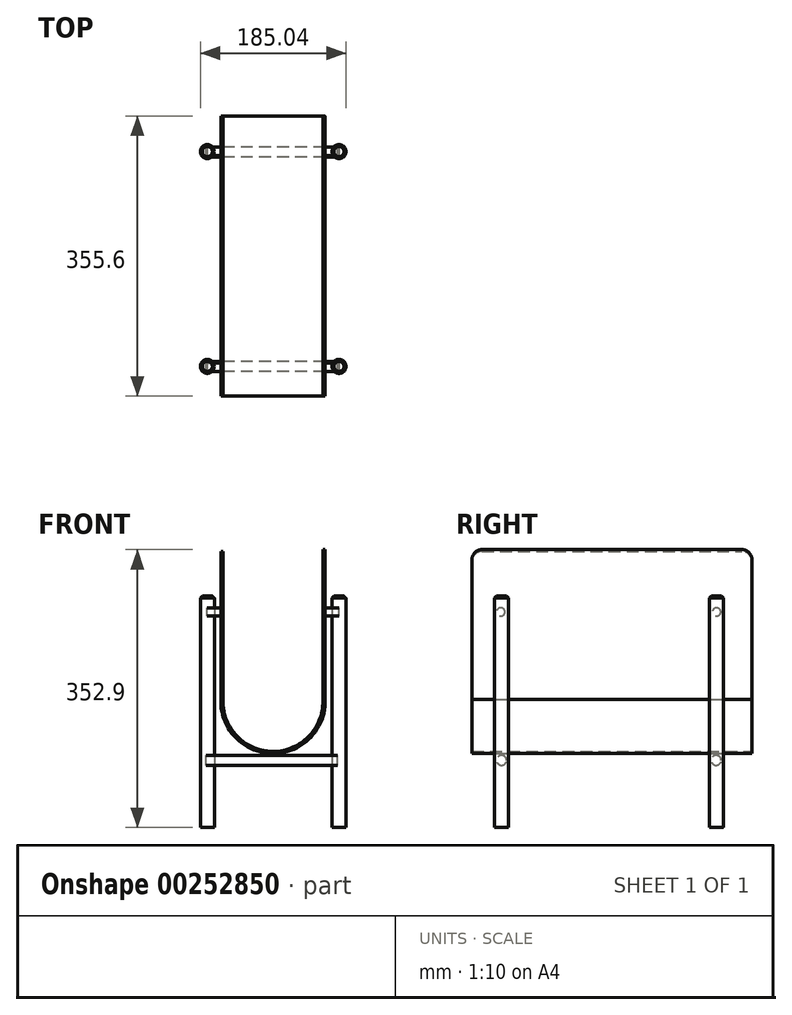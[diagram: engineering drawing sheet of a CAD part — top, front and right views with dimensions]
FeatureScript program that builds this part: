
annotation { "Feature Type Name" : "Feature", "Feature Type Description" : "" }
export const myFeature = defineFeature(function(context is Context, id is Id, definition is map)
    precondition{}
    {
        {
            var Q0;
            Q0=qCreatedBy(makeId("Front.planeOp"),FACE);
            var sketch = newSketch(context, id + "F0", { "sketchPlane" : qUnion([Q0])});
            skArc(sketch, "E0", {"start": v(-63.5, 63.5) * mm, "mid": v(1.2, 0.01) * mm, "end": v(63.46, 65.88) * mm});
            skLineSegment(sketch, "E1", {"start": v(-63.5, 63.5) * mm, "end": v(-63.5, 254) * mm});
            skLineSegment(sketch, "E2", {"start": v(63.46, 65.88) * mm, "end": v(63.46, 256.38) * mm});
            skLineSegment(sketch, "E3.0", {"start": v(-66.3, 63.5) * mm, "end": v(-66.3, 254) * mm});
            skArc(sketch, "E3.1", {"start": v(-66.3, 63.5) * mm, "mid": v(1.22, -2.78) * mm, "end": v(66.25, 65.94) * mm});
            skLineSegment(sketch, "E3.2", {"start": v(66.25, 65.94) * mm, "end": v(66.25, 256.32) * mm});
            skLineSegment(sketch, "E4", {"start": v(-66.3, 254) * mm, "end": v(-63.5, 254) * mm});
            skLineSegment(sketch, "E5", {"start": v(63.46, 256.38) * mm, "end": v(66.25, 256.32) * mm});
            skSolve(sketch);
        }
        {
            var Q0;
            Q0=makeQuery(id+"F0.imprint","IMPRINT",FACE,{"disambiguationData":[TD([[makeQuery(id+"F0.imprint","IMPRINT",EDGE,{"derivedFrom":sQuery(id+"F0.wireOp",EDGE,"E0")}),-1.0]])]});
            extrude(context, id + "F1", {"entities" : qUnion([Q0]), "depth" : 355.6 * mm});
        }
        {
            var Q0;
            Q0=makeQuery(id+"F1.opExtrude","CAP_EDGE",EDGE,{"disambiguationData":[OSD([sQuery(id+"F0.wireOp",EDGE,"E4")])],"isStart":false});
            var Q1;
            Q1=makeQuery(id+"F1.opExtrude","CAP_EDGE",EDGE,{"disambiguationData":[OSD([sQuery(id+"F0.wireOp",EDGE,"E5")])],"isStart":false});
            var Q2;
            Q2=makeQuery(id+"F1.opExtrude","CAP_EDGE",EDGE,{"disambiguationData":[OSD([sQuery(id+"F0.wireOp",EDGE,"E4")])],"isStart":true});
            var Q3;
            Q3=makeQuery(id+"F1.opExtrude","CAP_EDGE",EDGE,{"disambiguationData":[OSD([sQuery(id+"F0.wireOp",EDGE,"E5")])],"isStart":true});
            fillet(context, id + "F2", {"entities" : qUnion([Q0, Q1, Q2, Q3]), "radius" : 12.7 * mm, "tangentPropagation" : true, "allowEdgeOverflow" : false});
        }
        {
            var Q0;
            Q0=qCreatedBy(makeId("Top.planeOp"),FACE);
            var sketch = newSketch(context, id + "F3", { "sketchPlane" : qUnion([Q0])});
            skCircle(sketch, "E6", {"center": v(-83.41, -45.01) * mm, "radius": 8.9 * mm});
            skCircle(sketch, "E7", {"center": v(83.85, -45.01) * mm, "radius": 8.9 * mm});
            skCircle(sketch, "E8", {"center": v(-83.41, -317.88) * mm, "radius": 8.9 * mm});
            skCircle(sketch, "E9", {"center": v(83.85, -317.88) * mm, "radius": 8.9 * mm});
            skSolve(sketch);
        }
        {
            var Q0;
            Q0=makeQuery(id+"F3.imprint","IMPRINT",FACE,{"disambiguationData":[TD([[makeQuery(id+"F3.imprint","IMPRINT",EDGE,{"derivedFrom":sQuery(id+"F3.wireOp",EDGE,"E6")}),1.0]])]});
            var Q1;
            Q1=makeQuery(id+"F3.imprint","IMPRINT",FACE,{"disambiguationData":[TD([[makeQuery(id+"F3.imprint","IMPRINT",EDGE,{"derivedFrom":sQuery(id+"F3.wireOp",EDGE,"E8")}),1.0]])]});
            var Q2;
            Q2=makeQuery(id+"F3.imprint","IMPRINT",FACE,{"disambiguationData":[TD([[makeQuery(id+"F3.imprint","IMPRINT",EDGE,{"derivedFrom":sQuery(id+"F3.wireOp",EDGE,"E9")}),1.0]])]});
            var Q3;
            Q3=makeQuery(id+"F3.imprint","IMPRINT",FACE,{"disambiguationData":[TD([[makeQuery(id+"F3.imprint","IMPRINT",EDGE,{"derivedFrom":sQuery(id+"F3.wireOp",EDGE,"E7")}),1.0]])]});
            extrude(context, id + "F4", {"entities" : qUnion([Q0, Q1, Q2, Q3]), "depth" : 197.36 * mm, "hasSecondDirection" : true, "secondDirectionOppositeDirection" : true, "secondDirectionDepth" : 96.52 * mm});
        }
        {
            var Q0;
            Q0=qCreatedBy(makeId("Right.planeOp"),FACE);
            var sketch = newSketch(context, id + "F5", { "sketchPlane" : qUnion([Q0])});
            skCircle(sketch, "E10", {"center": v(-317.96, -11.33) * mm, "radius": 6.35 * mm});
            skCircle(sketch, "E11", {"center": v(-45.4, -11.33) * mm, "radius": 6.35 * mm});
            skSolve(sketch);
        }
        {
            var Q0;
            Q0 = qSketchRegion(id + "F5", true);
            extrude(context, id + "F6", {"entities" : qUnion([Q0]), "depth" : 82.04 * mm, "hasSecondDirection" : true, "secondDirectionOppositeDirection" : true, "secondDirectionDepth" : 84.84 * mm});
        }
        {
            var Q0;
            Q0=makeQuery(id+"F1.opExtrude","SWEPT_FACE",FACE,{"disambiguationData":[OSD([sQuery(id+"F0.wireOp",EDGE,"E3.2")])]});
            var sketch = newSketch(context, id + "F7", { "sketchPlane" : qUnion([Q0])});
            skCircle(sketch, "E12", {"center": v(-318.9, 177.16) * mm, "radius": 5.27 * mm});
            skCircle(sketch, "E13", {"center": v(-44.86, 177.16) * mm, "radius": 5.26 * mm});
            skSolve(sketch);
        }
        {
            var Q0;
            Q0 = qSketchRegion(id + "F7", true);
            extrude(context, id + "F8", {"entities" : qUnion([Q0]), "depth" : 17.78 * mm});
        }
        {
            var Q0;
            Q0=makeQuery(id+"F8.opExtrude","SWEPT_BODY",BODY,{"disambiguationData":[OSD([sQuery(id+"F7.wireOp",EDGE,"E13")])]});
            var Q1;
            Q1=makeQuery(id+"F8.opExtrude","SWEPT_BODY",BODY,{"disambiguationData":[OSD([sQuery(id+"F7.wireOp",EDGE,"E12")])]});
            var Q2;
            Q2=qCreatedBy(makeId("Right.planeOp"),FACE);
            mirror(context, id + "F9", {"entities" : qUnion([Q0, Q1]), "mirrorPlane" : qUnion([Q2])});
        }
        {
            var Q0;
            Q0=makeQuery(id+"F4.opExtrude","CAP_EDGE",EDGE,{"disambiguationData":[OSD([sQuery(id+"F3.wireOp",EDGE,"E6")])],"isStart":false});
            var Q1;
            Q1=makeQuery(id+"F4.opExtrude","CAP_EDGE",EDGE,{"disambiguationData":[OSD([sQuery(id+"F3.wireOp",EDGE,"E8")])],"isStart":false});
            var Q2;
            Q2=makeQuery(id+"F4.opExtrude","CAP_EDGE",EDGE,{"disambiguationData":[OSD([sQuery(id+"F3.wireOp",EDGE,"E9")])],"isStart":false});
            var Q3;
            Q3=makeQuery(id+"F4.opExtrude","CAP_EDGE",EDGE,{"disambiguationData":[OSD([sQuery(id+"F3.wireOp",EDGE,"E7")])],"isStart":false});
            chamfer(context, id + "F10", {"entities" : qUnion([Q0, Q1, Q2, Q3]), "width" : 2.54 * mm, "tangentPropagation" : true});
        }
    });
